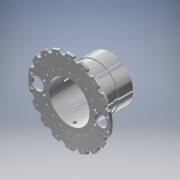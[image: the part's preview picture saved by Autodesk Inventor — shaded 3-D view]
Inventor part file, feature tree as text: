
AUTODESK INVENTOR PART (.ipt)
format: ipt  version: 2016 (Build 200138000, 138)  size: 382,464 bytes
history: native  units: mm
features: sketch x9, extrude x6, hole x5, pattern_circular x3, projected_geometry x3, plane x2, mirror x2, fillet x1
ambient origin geometry x8: Origin, YZ Plane, XZ Plane, XY Plane, X Axis, Y Axis, Z Axis, Center Point
bodies: Solid1 (feature_tree)
feature tree (31):
  sketch  "Sketch1"  dims[d0=151.2mm d1=76.6mm]
  extrude  "Extrusion1"  Depth=76.6mm
  extrude  "Extrusion2"  Depth=3.0mm
  plane  "Work Plane1"
  extrude  "Extrusion3"  Depth=23.0mm
  extrude  "Extrusion4"  Depth=28.3mm
  pattern_circular  "Circular Pattern1"  [2 undecoded]
  fillet  "Fillet1"  Radius=1.5mm
  hole  "Hole1"  [1 undecoded]
  extrude  "Extrusion5"  Depth=6.0mm
  hole  "Hole2"  [1 undecoded]
  hole  "Hole3"  [1 undecoded]
  plane  "Work Plane2"
  hole  "Hole4"  [1 undecoded]
  extrude  "Extrusion6"  Depth=10.0mm TaperAngle=0.0deg
  pattern_circular  "Circular Pattern2"  [2 undecoded]
  mirror  "Mirror2"
  mirror  "Mirror3"
  sketch  "Sketch10"  dims[d12=3.0mm d13=36.0mm d14=1.5mm d15=10.0mm d16=0.0mm d17=0.698132mm d18=48.0mm d19=0.0mm d20=60.0mm d21=360.0deg d23=2.6mm d24=6.0mm d25=4.0mm d26=2.0mm d27=90.0deg d28=8.0mm d29=20.594885mm d30=23.0mm d31=10.0mm d32=0.0mm d33=5.4mm d34=6.0mm d35=4.0mm d36=2.0mm d37=90.0deg d38=3.0mm d39=20.594885mm d40=6.0mm d41=3.0mm d42=40.0mm d44=60.0deg d46=40.0mm d48=60.0deg d50=3.1mm d51=6.0mm d52=4.0mm d53=2.0mm d54=90.0deg d55=8.0mm d56=20.594885mm d57=6.0mm d58=6.0mm d59=6.0mm d60=4.0mm d61=2.0mm d62=90.0deg d63=8.0mm d64=20.594885mm d65=12.0mm d66=1.745329mm d67=10.0mm d68=0.0mm d69=40.0mm d70=60.0deg d74=18.0mm d76=6.5mm d78=9.5mm d79=12.8mm d80=3.3mm d81=4.0mm d82=1.5mm d83=6.5mm d84=2.1mm d85=6.0mm d86=4.0mm d87=2.0mm d88=90.0deg d89=8.0mm d90=20.594885mm d91=20.0mm d92=360.0deg d97=66.0mm d99=50.9mm]
  sketch  "Sketch9"  dims[d11=0.0mm]
  hole  "Hole5"  [1 undecoded]
  pattern_circular  "Circular Pattern3"  [2 undecoded]
  sketch  "Sketch2"  dims[d2=3.0mm d3=74.6mm]
  sketch  "Sketch3"  dims[d4=23.0mm d5=23.0mm]
  sketch  "Sketch4"  dims[d6=28.3mm d7=28.3mm]
  sketch  "Sketch5"  dims[d8=4.5mm]
  projected_geometry  "Projected Loop1"
  sketch  "Sketch6"  dims[d9=0.0mm]
  sketch  "Sketch7"  dims[d10=72.0mm]
  projected_geometry  "Project Cut Edges1"
  projected_geometry  "Project Cut Edges2"
note: 11 required parameter values undecoded (feature->parameter linkage not recoverable at this tier; creation-order binding heuristic only, values carry confidence <= 0.55)
